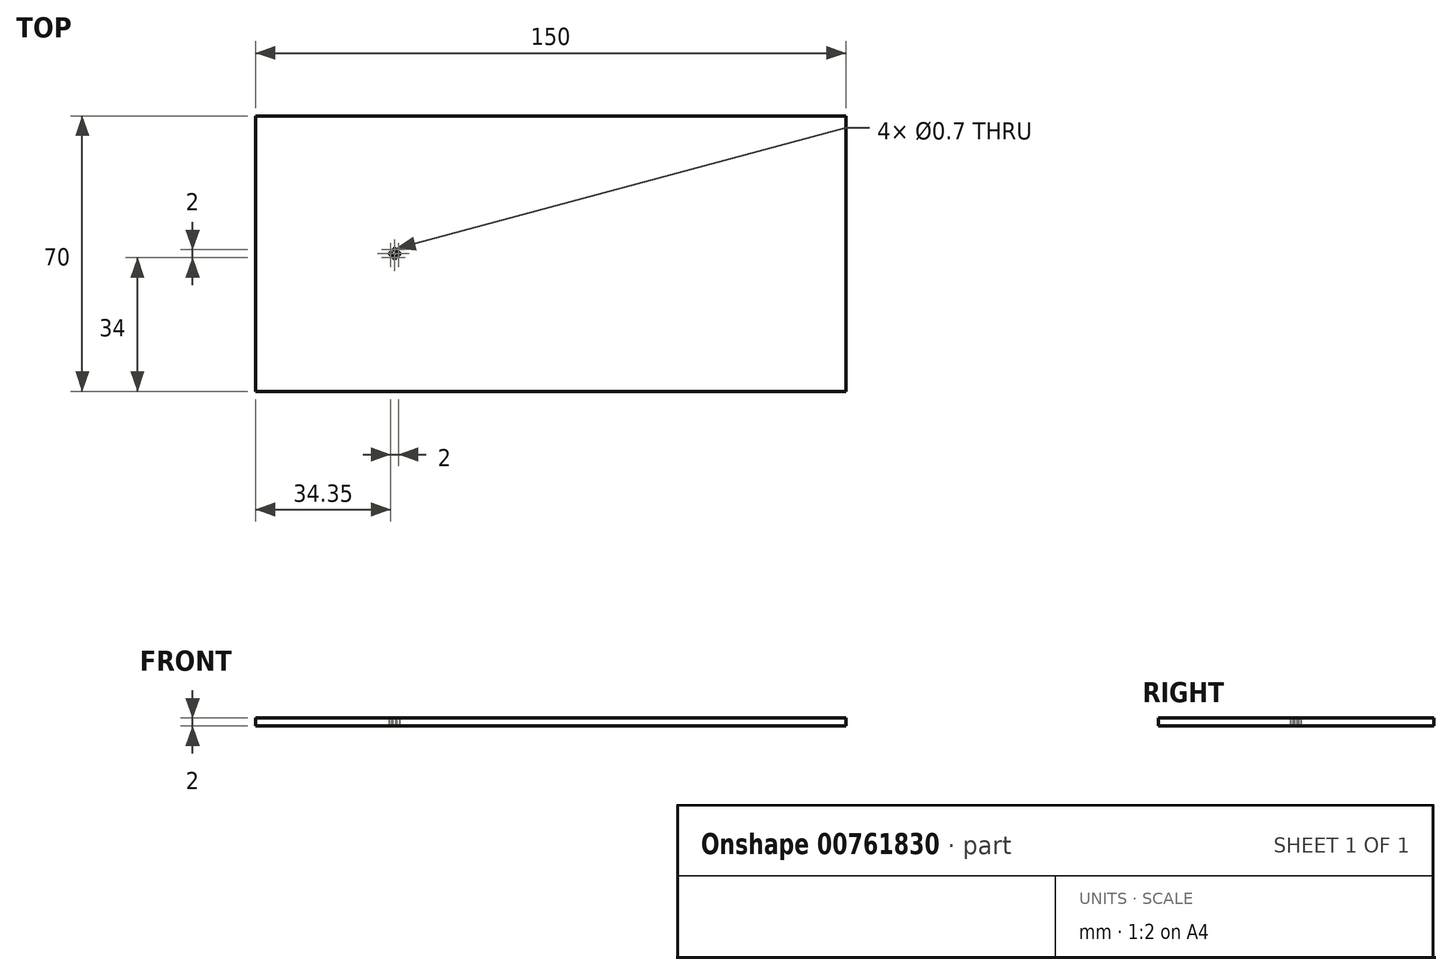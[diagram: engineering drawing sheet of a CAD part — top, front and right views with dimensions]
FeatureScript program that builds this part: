
annotation { "Feature Type Name" : "Feature", "Feature Type Description" : "" }
export const myFeature = defineFeature(function(context is Context, id is Id, definition is map)
    precondition{}
    {
        {
            var Q0;
            Q0=qCreatedBy(makeId("Top.planeOp"),FACE);
            var sketch = newSketch(context, id + "F0", { "sketchPlane" : qUnion([Q0])});
            skLineSegment(sketch, "E0.bottom", {"start": v(77.15, 35) * mm, "end": v(-72.85, 35) * mm});
            skLineSegment(sketch, "E0.top", {"start": v(77.15, -35) * mm, "end": v(-72.85, -35) * mm});
            skLineSegment(sketch, "E0.left", {"start": v(77.15, 35) * mm, "end": v(77.15, -35) * mm});
            skLineSegment(sketch, "E0.right", {"start": v(-72.85, 35) * mm, "end": v(-72.85, -35) * mm});
            skPoint(sketch, "E0.middle", {"position": v(2.15, 0) * mm});
            skSolve(sketch);
        }
        {
            var Q0;
            Q0 = qSketchRegion(id + "F0", true);
            extrude(context, id + "F1", {"entities" : qUnion([Q0]), "depth" : 2 * mm, "offsetDistance" : 25 * mm});
        }
        {
            var Q0;
            Q0=makeQuery(id+"F1.opExtrude","CAP_FACE",FACE,{"disambiguationData":[OSD([sQuery(id+"F0.wireOp",EDGE,"E0.bottom"),sQuery(id+"F0.wireOp",EDGE,"E0.top"),sQuery(id+"F0.wireOp",EDGE,"E0.left"),sQuery(id+"F0.wireOp",EDGE,"E0.right")])],"isStart":false});
            var sketch = newSketch(context, id + "F2", { "sketchPlane" : qUnion([Q0])});
            skPoint(sketch, "E1", {"position": v(-37.5, 0) * mm});
            skCircle(sketch, "E2", {"center": v(-37.5, 1) * mm, "radius": 0.35 * mm});
            skCircle(sketch, "E3", {"center": v(-36.5, 0) * mm, "radius": 0.35 * mm});
            skCircle(sketch, "E4", {"center": v(-37.5, -1) * mm, "radius": 0.35 * mm});
            skCircle(sketch, "E5", {"center": v(-38.5, 0) * mm, "radius": 0.35 * mm});
            skSolve(sketch);
        }
        {
            var Q0;
            Q0 = qSketchRegion(id + "F2", true);
            extrude(context, id + "F3", {"entities" : qUnion([Q0]), "operationType" : NewBodyOperationType.REMOVE, "oppositeDirection" : true, "depth" : 25 * mm, "offsetDistance" : 25 * mm});
        }
    });
